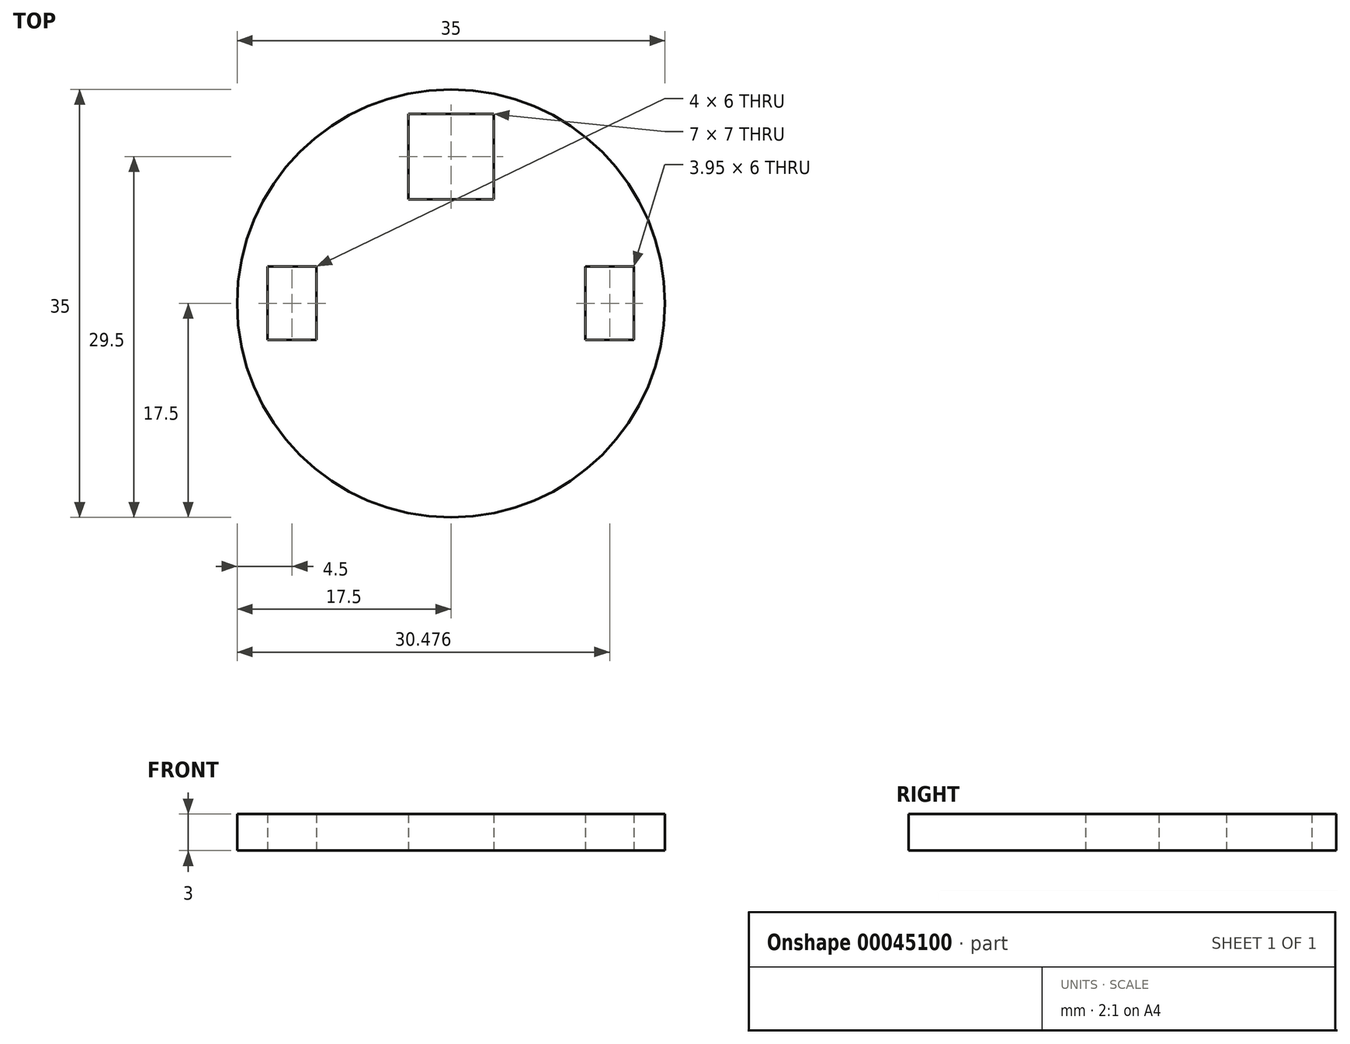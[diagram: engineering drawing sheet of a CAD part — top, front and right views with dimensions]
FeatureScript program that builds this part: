
annotation { "Feature Type Name" : "Feature", "Feature Type Description" : "" }
export const myFeature = defineFeature(function(context is Context, id is Id, definition is map)
    precondition{}
    {
        {
            var Q0;
            Q0=qCreatedBy(makeId("Top.planeOp"),FACE);
            var sketch = newSketch(context, id + "F0", { "sketchPlane" : qUnion([Q0])});
            skCircle(sketch, "E0", {"center": v(0, 0) * mm, "radius": 17.5 * mm});
            skLineSegment(sketch, "E1.bottom", {"start": v(-15, 3) * mm, "end": v(-11, 3) * mm});
            skLineSegment(sketch, "E1.top", {"start": v(-15, -3) * mm, "end": v(-11, -3) * mm});
            skLineSegment(sketch, "E1.left", {"start": v(-15, 3) * mm, "end": v(-15, -3) * mm});
            skLineSegment(sketch, "E1.right", {"start": v(-11, 3) * mm, "end": v(-11, -3) * mm});
            skLineSegment(sketch, "E2.bottom", {"start": v(14.95, 3) * mm, "end": v(11, 3) * mm});
            skLineSegment(sketch, "E2.top", {"start": v(14.95, -3) * mm, "end": v(11, -3) * mm});
            skLineSegment(sketch, "E2.left", {"start": v(14.95, 3) * mm, "end": v(14.95, -3) * mm});
            skLineSegment(sketch, "E2.right", {"start": v(11, 3) * mm, "end": v(11, -3) * mm});
            skLineSegment(sketch, "E3.bottom", {"start": v(-3.5, 15.5) * mm, "end": v(3.5, 15.5) * mm});
            skLineSegment(sketch, "E3.top", {"start": v(-3.5, 8.5) * mm, "end": v(3.5, 8.5) * mm});
            skLineSegment(sketch, "E3.left", {"start": v(-3.5, 15.5) * mm, "end": v(-3.5, 8.5) * mm});
            skLineSegment(sketch, "E3.right", {"start": v(3.5, 15.5) * mm, "end": v(3.5, 8.5) * mm});
            skSolve(sketch);
        }
        {
            var Q0;
            Q0=makeQuery(id+"F0.imprint","IMPRINT",FACE,{"disambiguationData":[TD([[makeQuery(id+"F0.imprint","IMPRINT",EDGE,{"derivedFrom":sQuery(id+"F0.wireOp",EDGE,"E0")}),1.0]])]});
            extrude(context, id + "F1", {"entities" : qUnion([Q0]), "depth" : 3 * mm});
        }
    });
